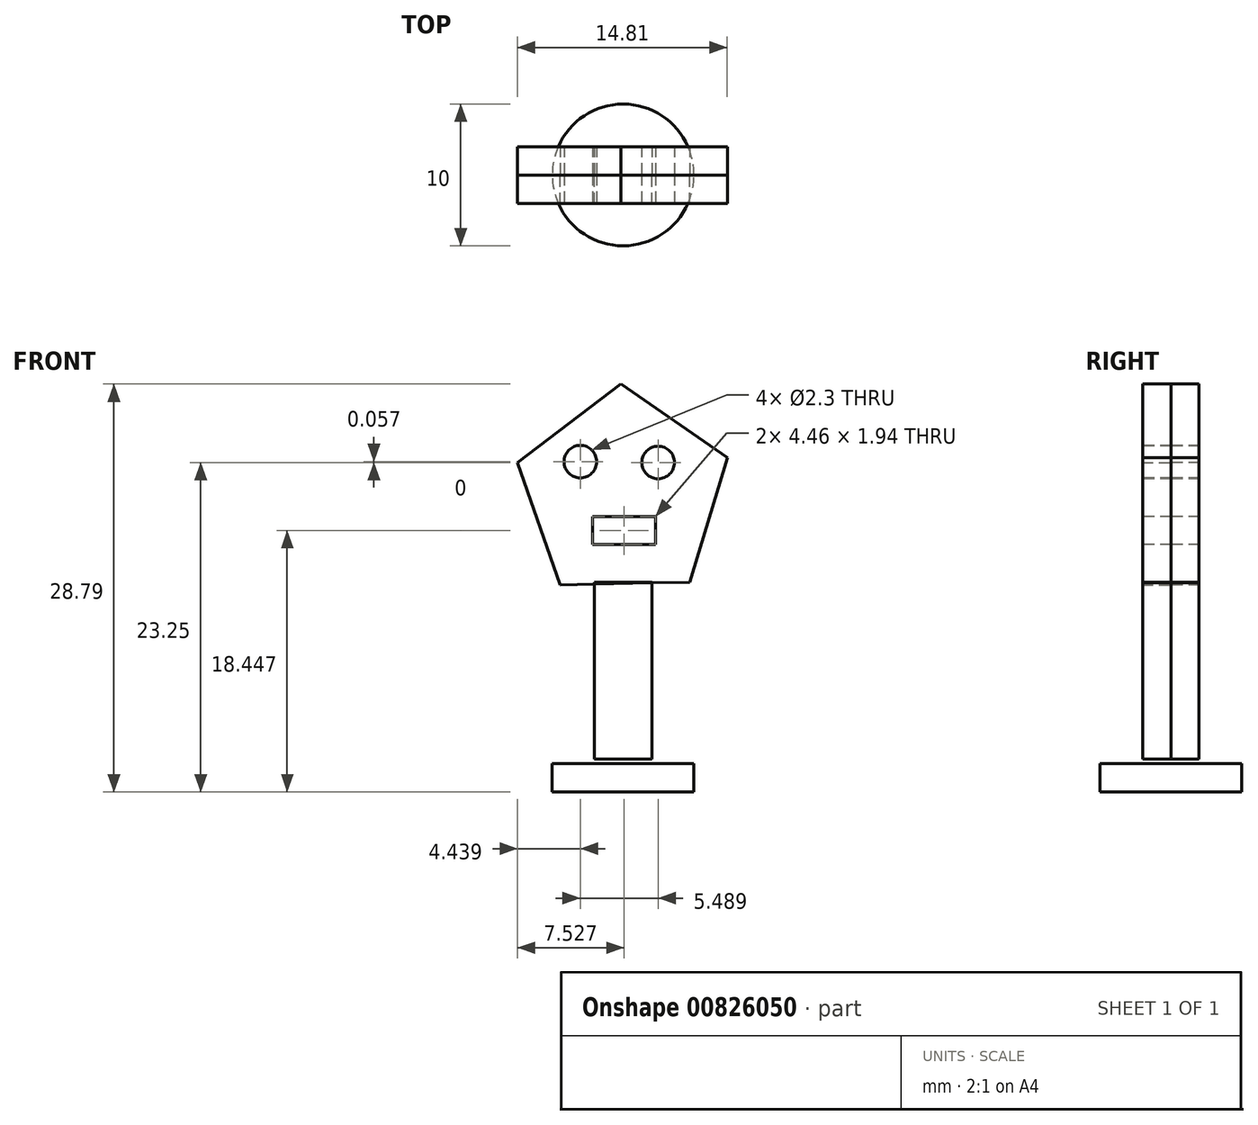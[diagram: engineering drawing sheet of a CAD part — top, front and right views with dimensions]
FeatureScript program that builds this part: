
annotation { "Feature Type Name" : "Feature", "Feature Type Description" : "" }
export const myFeature = defineFeature(function(context is Context, id is Id, definition is map)
    precondition{}
    {
        {
            var Q0;
            Q0=qCreatedBy(makeId("Top.planeOp"),FACE);
            var sketch = newSketch(context, id + "F0", { "sketchPlane" : qUnion([Q0])});
            skCircle(sketch, "E0", {"center": v(0, 0) * mm, "radius": 5 * mm});
            skSolve(sketch);
        }
        {
            var Q0;
            Q0 = qSketchRegion(id + "F0", true);
            extrude(context, id + "F1", {"entities" : qUnion([Q0]), "depth" : 2 * mm, "offsetDistance" : 25 * mm});
        }
        {
            var Q0;
            Q0=qCreatedBy(makeId("Front.planeOp"),FACE);
            var sketch = newSketch(context, id + "F2", { "sketchPlane" : qUnion([Q0])});
            skLineSegment(sketch, "E1.bottom", {"start": v(-2.02, 14.8) * mm, "end": v(2.02, 14.8) * mm});
            skLineSegment(sketch, "E1.top", {"start": v(-2.02, 2.3) * mm, "end": v(2.02, 2.3) * mm});
            skLineSegment(sketch, "E1.left", {"start": v(-2.02, 14.8) * mm, "end": v(-2.02, 2.3) * mm});
            skLineSegment(sketch, "E1.right", {"start": v(2.02, 14.8) * mm, "end": v(2.02, 2.3) * mm});
            skCircle(sketch, "E2.cCircle", {"center": v(0, 21) * mm, "radius": 6.3 * mm, "construction": true});
            skLineSegment(sketch, "E2.0", {"start": v(7.35, 23.57) * mm, "end": v(4.71, 14.8) * mm});
            skLineSegment(sketch, "E2.1", {"start": v(4.71, 14.8) * mm, "end": v(-4.44, 14.61) * mm});
            skLineSegment(sketch, "E2.2", {"start": v(-4.44, 14.61) * mm, "end": v(-7.46, 23.25) * mm});
            skLineSegment(sketch, "E2.3", {"start": v(-7.46, 23.25) * mm, "end": v(-0.17, 28.8) * mm});
            skLineSegment(sketch, "E2.4", {"start": v(-0.17, 28.8) * mm, "end": v(7.35, 23.57) * mm});
            skPoint(sketch, "E2.0.midPoint", {"position": v(6.03, 19.19) * mm});
            skSolve(sketch);
        }
        {
            var Q0;
            {var subQ0=sQuery(id+"F2.wireOp",EDGE,"E1.top");Q0=makeQuery(id+"F2.imprint","IMPRINT",FACE,{"disambiguationData":[TD([[makeQuery(id+"F2.imprint","IMPRINT",EDGE,{"derivedFrom":subQ0}),1.0]])]});}
            var Q1;
            {var subQ2=sQuery(id+"F2.wireOp",EDGE,"E1.bottom");Q1=makeQuery(id+"F2.imprint","IMPRINT",FACE,{"disambiguationData":[TD([[makeQuery(id+"F2.imprint","IMPRINT",EDGE,{"derivedFrom":subQ2}),1.0]])]});}
            extrude(context, id + "F3", {"entities" : qUnion([Q0, Q1]), "depth" : 2 * mm, "offsetDistance" : 25 * mm});
        }
        {
            var Q0;
            Q0=makeQuery(id+"F3.opExtrude","CAP_FACE",FACE,{"disambiguationData":[OSD([sQuery(id+"F2.wireOp",EDGE,"E1.top"),sQuery(id+"F2.wireOp",EDGE,"E1.left"),sQuery(id+"F2.wireOp",EDGE,"E1.right"),sQuery(id+"F2.wireOp",EDGE,"E2.1")])],"isStart":true});
            var Q1;
            Q1=makeQuery(id+"F3.opExtrude","CAP_FACE",FACE,{"disambiguationData":[OSD([sQuery(id+"F2.wireOp",EDGE,"E1.bottom"),sQuery(id+"F2.wireOp",EDGE,"E1.left"),sQuery(id+"F2.wireOp",EDGE,"E1.right"),sQuery(id+"F2.wireOp",EDGE,"E2.0"),sQuery(id+"F2.wireOp",EDGE,"E2.1"),sQuery(id+"F2.wireOp",EDGE,"E2.2"),sQuery(id+"F2.wireOp",EDGE,"E2.3"),sQuery(id+"F2.wireOp",EDGE,"E2.4")])],"isStart":true});
            extrude(context, id + "F4", {"entities" : qUnion([Q0, Q1]), "depth" : 2 * mm, "offsetDistance" : 25 * mm});
        }
        {
            var Q0;
            Q0=makeQuery(id+"F3.opExtrude","CAP_FACE",FACE,{"disambiguationData":[OSD([sQuery(id+"F2.wireOp",EDGE,"E1.bottom"),sQuery(id+"F2.wireOp",EDGE,"E1.left"),sQuery(id+"F2.wireOp",EDGE,"E1.right"),sQuery(id+"F2.wireOp",EDGE,"E2.0"),sQuery(id+"F2.wireOp",EDGE,"E2.1"),sQuery(id+"F2.wireOp",EDGE,"E2.2"),sQuery(id+"F2.wireOp",EDGE,"E2.3"),sQuery(id+"F2.wireOp",EDGE,"E2.4")])],"isStart":false});
            var sketch = newSketch(context, id + "F5", { "sketchPlane" : qUnion([Q0])});
            skCircle(sketch, "E3", {"center": v(-3.02, 23.3) * mm, "radius": 1.15 * mm});
            skCircle(sketch, "E4", {"center": v(2.47, 23.25) * mm, "radius": 1.15 * mm});
            skLineSegment(sketch, "E5.bottom", {"start": v(-2.16, 19.42) * mm, "end": v(2.3, 19.42) * mm});
            skLineSegment(sketch, "E5.top", {"start": v(-2.16, 17.48) * mm, "end": v(2.3, 17.48) * mm});
            skLineSegment(sketch, "E5.left", {"start": v(-2.16, 19.42) * mm, "end": v(-2.16, 17.48) * mm});
            skLineSegment(sketch, "E5.right", {"start": v(2.3, 19.42) * mm, "end": v(2.3, 17.48) * mm});
            skSolve(sketch);
        }
        {
            var Q0;
            Q0=makeQuery(id+"F5.imprint","IMPRINT",FACE,{"disambiguationData":[TD([[makeQuery(id+"F5.imprint","IMPRINT",EDGE,{"derivedFrom":sQuery(id+"F5.wireOp",EDGE,"E3")}),1.0]])]});
            var Q1;
            Q1=makeQuery(id+"F5.imprint","IMPRINT",FACE,{"disambiguationData":[TD([[makeQuery(id+"F5.imprint","IMPRINT",EDGE,{"derivedFrom":sQuery(id+"F5.wireOp",EDGE,"E4")}),1.0]])]});
            var Q2;
            Q2=makeQuery(id+"F5.imprint","IMPRINT",FACE,{"disambiguationData":[TD([[makeQuery(id+"F5.imprint","IMPRINT",EDGE,{"derivedFrom":sQuery(id+"F5.wireOp",EDGE,"E5.bottom")}),-1.0]])]});
            extrude(context, id + "F6", {"entities" : qUnion([Q0, Q1, Q2]), "operationType" : NewBodyOperationType.REMOVE, "oppositeDirection" : true, "depth" : 4 * mm, "offsetDistance" : 25 * mm});
        }
    });
